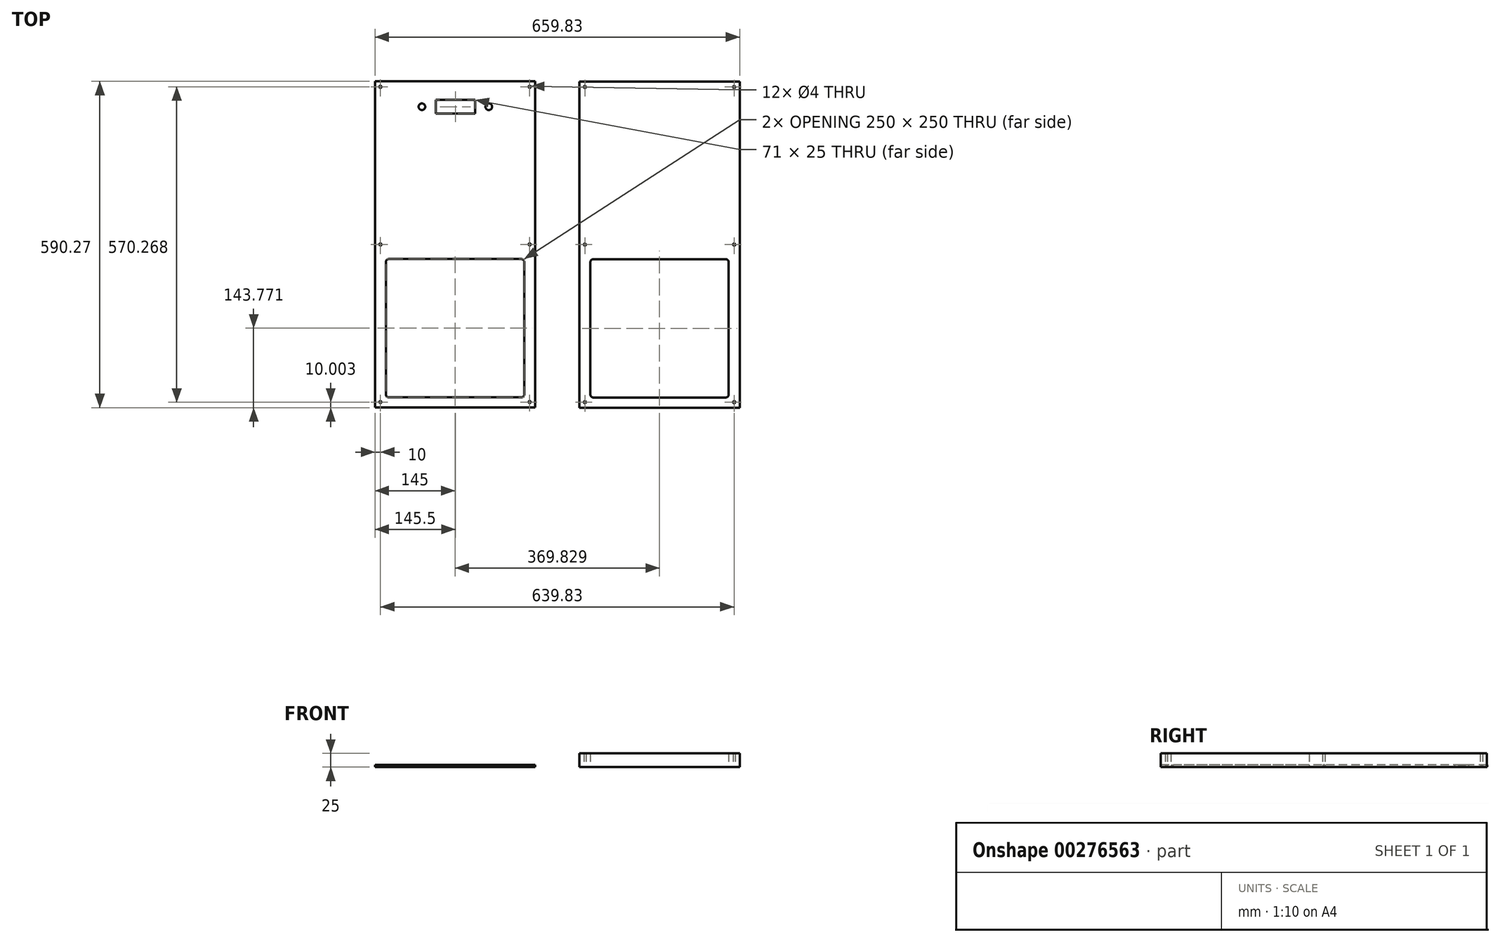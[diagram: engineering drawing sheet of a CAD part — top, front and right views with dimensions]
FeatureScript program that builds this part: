
annotation { "Feature Type Name" : "Feature", "Feature Type Description" : "" }
export const myFeature = defineFeature(function(context is Context, id is Id, definition is map)
    precondition{}
    {
        {
            var Q0;
            Q0=qCreatedBy(makeId("Top.planeOp"),FACE);
            var sketch = newSketch(context, id + "F0", { "sketchPlane" : qUnion([Q0])});
            skLineSegment(sketch, "E0.bottom", {"start": v(-206, 398.8) * mm, "end": v(84, 398.8) * mm});
            skLineSegment(sketch, "E0.top", {"start": v(-206, -191.2) * mm, "end": v(84, -191.2) * mm});
            skLineSegment(sketch, "E0.left", {"start": v(-206, 398.8) * mm, "end": v(-206, -191.2) * mm});
            skLineSegment(sketch, "E0.right", {"start": v(84, 398.8) * mm, "end": v(84, -191.2) * mm});
            skLineSegment(sketch, "E1.bottom", {"start": v(-186, 77.3) * mm, "end": v(64, 77.3) * mm});
            skLineSegment(sketch, "E1.top", {"start": v(-186, -172.7) * mm, "end": v(64, -172.7) * mm});
            skLineSegment(sketch, "E1.left", {"start": v(-186, 77.3) * mm, "end": v(-186, -172.7) * mm});
            skLineSegment(sketch, "E1.right", {"start": v(64, 77.3) * mm, "end": v(64, -172.7) * mm});
            skLineSegment(sketch, "E2.bottom", {"start": v(-96, 365.3) * mm, "end": v(-25, 365.3) * mm});
            skLineSegment(sketch, "E2.top", {"start": v(-96, 340.3) * mm, "end": v(-25, 340.3) * mm});
            skLineSegment(sketch, "E2.left", {"start": v(-96, 365.3) * mm, "end": v(-96, 340.3) * mm});
            skLineSegment(sketch, "E2.right", {"start": v(-25, 365.3) * mm, "end": v(-25, 340.3) * mm});
            skCircle(sketch, "E3", {"center": v(0, 352.8) * mm, "radius": 6 * mm});
            skCircle(sketch, "E4", {"center": v(-121, 352.8) * mm, "radius": 6 * mm});
            skSolve(sketch);
        }
        {
            var Q0;
            Q0 = qSketchRegion(id + "F0", true);
            extrude(context, id + "F1", {"entities" : qUnion([Q0]), "depth" : 4 * mm, "offsetDistance" : 25 * mm});
        }
        {
            var Q0;
            Q0=makeQuery(id+"F1.opExtrude","CAP_FACE",FACE,{"disambiguationData":[OSD([sQuery(id+"F0.wireOp",EDGE,"E0.bottom"),sQuery(id+"F0.wireOp",EDGE,"E0.top"),sQuery(id+"F0.wireOp",EDGE,"E0.left"),sQuery(id+"F0.wireOp",EDGE,"E0.right"),sQuery(id+"F0.wireOp",EDGE,"E1.bottom"),sQuery(id+"F0.wireOp",EDGE,"E1.top"),sQuery(id+"F0.wireOp",EDGE,"E1.left"),sQuery(id+"F0.wireOp",EDGE,"E1.right"),sQuery(id+"F0.wireOp",EDGE,"E2.bottom"),sQuery(id+"F0.wireOp",EDGE,"E2.top"),sQuery(id+"F0.wireOp",EDGE,"E2.left"),sQuery(id+"F0.wireOp",EDGE,"E2.right"),sQuery(id+"F0.wireOp",EDGE,"E3"),sQuery(id+"F0.wireOp",EDGE,"E4")])],"isStart":false});
            var sketch = newSketch(context, id + "F2", { "sketchPlane" : qUnion([Q0])});
            skPoint(sketch, "E5", {"position": v(-196, -181.2) * mm});
            skPoint(sketch, "E6", {"position": v(74, -181.2) * mm});
            skPoint(sketch, "E7", {"position": v(74, 103.8) * mm});
            skPoint(sketch, "E8", {"position": v(74, 388.8) * mm});
            skPoint(sketch, "E9", {"position": v(-196, 103.8) * mm});
            skPoint(sketch, "E10", {"position": v(-196, 388.8) * mm});
            skSolve(sketch);
        }
        {
            var Q0;
            Q0=sQuery(id+"F2.wireOp",VERTEX,"E10");
            var Q1;
            Q1=sQuery(id+"F2.wireOp",VERTEX,"E8");
            var Q2;
            Q2=sQuery(id+"F2.wireOp",VERTEX,"E7");
            var Q3;
            Q3=sQuery(id+"F2.wireOp",VERTEX,"E9");
            var Q4;
            Q4=sQuery(id+"F2.wireOp",VERTEX,"E5");
            var Q5;
            Q5=sQuery(id+"F2.wireOp",VERTEX,"E6");
            var Q6;
            Q6=makeQuery(id+"F1.opExtrude","SWEPT_BODY",BODY,{"disambiguationData":[OSD([sQuery(id+"F0.wireOp",EDGE,"E0.bottom"),sQuery(id+"F0.wireOp",EDGE,"E0.top"),sQuery(id+"F0.wireOp",EDGE,"E0.left"),sQuery(id+"F0.wireOp",EDGE,"E0.right"),sQuery(id+"F0.wireOp",EDGE,"E1.bottom"),sQuery(id+"F0.wireOp",EDGE,"E1.top"),sQuery(id+"F0.wireOp",EDGE,"E1.left"),sQuery(id+"F0.wireOp",EDGE,"E1.right"),sQuery(id+"F0.wireOp",EDGE,"E2.bottom"),sQuery(id+"F0.wireOp",EDGE,"E2.top"),sQuery(id+"F0.wireOp",EDGE,"E2.left"),sQuery(id+"F0.wireOp",EDGE,"E2.right"),sQuery(id+"F0.wireOp",EDGE,"E3"),sQuery(id+"F0.wireOp",EDGE,"E4")])]});
            hole(context, id + "F3", {"style" : HoleStyle.SIMPLE, "endStyle" : HoleEndStyle.THROUGH, "holeDiameter" : 4 * mm, "majorDiameter" : 5 * mm, "tappedDepth" : 12 * mm, "tapClearance" : 3, "locations" : qUnion([Q0, Q1, Q2, Q3, Q4, Q5]), "scope" : qUnion([Q6])});
        }
        {
            var Q0;
            Q0=qCreatedBy(makeId("Top.planeOp"),FACE);
            var sketch = newSketch(context, id + "F4", { "sketchPlane" : qUnion([Q0])});
            skLineSegment(sketch, "E11.bottom", {"start": v(163.83, 398.53) * mm, "end": v(453.83, 398.53) * mm});
            skLineSegment(sketch, "E11.top", {"start": v(163.83, -191.47) * mm, "end": v(453.83, -191.47) * mm});
            skLineSegment(sketch, "E11.left", {"start": v(163.83, 398.53) * mm, "end": v(163.83, -191.47) * mm});
            skLineSegment(sketch, "E11.right", {"start": v(453.83, 398.53) * mm, "end": v(453.83, -191.47) * mm});
            skLineSegment(sketch, "E12.bottom", {"start": v(183.83, 77.03) * mm, "end": v(433.83, 77.03) * mm});
            skLineSegment(sketch, "E12.top", {"start": v(183.83, -172.97) * mm, "end": v(433.83, -172.97) * mm});
            skLineSegment(sketch, "E12.left", {"start": v(183.83, 77.03) * mm, "end": v(183.83, -172.97) * mm});
            skLineSegment(sketch, "E12.right", {"start": v(433.83, 77.03) * mm, "end": v(433.83, -172.97) * mm});
            skPoint(sketch, "E13", {"position": v(173.83, 103.53) * mm});
            skSolve(sketch);
        }
        {
            var Q0;
            Q0 = qSketchRegion(id + "F4", true);
            extrude(context, id + "F5", {"entities" : qUnion([Q0]), "depth" : 25 * mm, "offsetDistance" : 25 * mm});
        }
        {
            var Q0;
            Q0=makeQuery(id+"F5.opExtrude","CAP_FACE",FACE,{"disambiguationData":[OSD([sQuery(id+"F4.wireOp",EDGE,"E11.bottom"),sQuery(id+"F4.wireOp",EDGE,"E11.top"),sQuery(id+"F4.wireOp",EDGE,"E11.left"),sQuery(id+"F4.wireOp",EDGE,"E11.right"),sQuery(id+"F4.wireOp",EDGE,"E12.bottom"),sQuery(id+"F4.wireOp",EDGE,"E12.top"),sQuery(id+"F4.wireOp",EDGE,"E12.left"),sQuery(id+"F4.wireOp",EDGE,"E12.right")])],"isStart":false});
            var sketch = newSketch(context, id + "F6", { "sketchPlane" : qUnion([Q0])});
            skPoint(sketch, "E14", {"position": v(173.83, 388.53) * mm});
            skPoint(sketch, "E15", {"position": v(443.83, 388.53) * mm});
            skPoint(sketch, "E16", {"position": v(443.83, 103.53) * mm});
            skPoint(sketch, "E17", {"position": v(443.83, -181.47) * mm});
            skPoint(sketch, "E18", {"position": v(173.83, -181.47) * mm});
            skPoint(sketch, "E19", {"position": v(173.83, 103.53) * mm});
            skSolve(sketch);
        }
        {
            var Q0;
            Q0=sQuery(id+"F6.wireOp",VERTEX,"E14");
            var Q1;
            Q1=sQuery(id+"F6.wireOp",VERTEX,"E15");
            var Q2;
            Q2=sQuery(id+"F6.wireOp",VERTEX,"E16");
            var Q3;
            Q3=sQuery(id+"F6.wireOp",VERTEX,"E19");
            var Q4;
            Q4=sQuery(id+"F6.wireOp",VERTEX,"E18");
            var Q5;
            Q5=sQuery(id+"F6.wireOp",VERTEX,"E17");
            var Q6;
            Q6=makeQuery(id+"F5.opExtrude","SWEPT_BODY",BODY,{"disambiguationData":[OSD([sQuery(id+"F4.wireOp",EDGE,"E11.bottom"),sQuery(id+"F4.wireOp",EDGE,"E11.top"),sQuery(id+"F4.wireOp",EDGE,"E11.left"),sQuery(id+"F4.wireOp",EDGE,"E11.right"),sQuery(id+"F4.wireOp",EDGE,"E12.bottom"),sQuery(id+"F4.wireOp",EDGE,"E12.top"),sQuery(id+"F4.wireOp",EDGE,"E12.left"),sQuery(id+"F4.wireOp",EDGE,"E12.right")])]});
            hole(context, id + "F7", {"style" : HoleStyle.SIMPLE, "endStyle" : HoleEndStyle.THROUGH, "holeDiameter" : 4 * mm, "majorDiameter" : 5 * mm, "tappedDepth" : 12 * mm, "tapClearance" : 3, "locations" : qUnion([Q0, Q1, Q2, Q3, Q4, Q5]), "scope" : qUnion([Q6])});
        }
        {
            var Q0;
            Q0=makeQuery(id+"F5.opExtrude","SWEPT_EDGE",EDGE,{"disambiguationData":[OSD([sQuery(id+"F4.wireOp",EDGE,"E12.bottom"),sQuery(id+"F4.wireOp",EDGE,"E12.right")])]});
            var Q1;
            Q1=makeQuery(id+"F5.opExtrude","SWEPT_EDGE",EDGE,{"disambiguationData":[OSD([sQuery(id+"F4.wireOp",EDGE,"E12.bottom"),sQuery(id+"F4.wireOp",EDGE,"E12.left")])]});
            var Q2;
            Q2=makeQuery(id+"F5.opExtrude","SWEPT_EDGE",EDGE,{"disambiguationData":[OSD([sQuery(id+"F4.wireOp",EDGE,"E12.top"),sQuery(id+"F4.wireOp",EDGE,"E12.right")])]});
            var Q3;
            Q3=makeQuery(id+"F5.opExtrude","SWEPT_EDGE",EDGE,{"disambiguationData":[OSD([sQuery(id+"F4.wireOp",EDGE,"E12.top"),sQuery(id+"F4.wireOp",EDGE,"E12.left")])]});
            fillet(context, id + "F8", {"entities" : qUnion([Q0, Q1, Q2, Q3]), "radius" : 5 * mm, "tangentPropagation" : true, "allowEdgeOverflow" : false});
        }
        {
            var Q0;
            Q0=makeQuery(id+"F1.opExtrude","SWEPT_EDGE",EDGE,{"disambiguationData":[OSD([sQuery(id+"F0.wireOp",EDGE,"E1.bottom"),sQuery(id+"F0.wireOp",EDGE,"E1.right")])]});
            var Q1;
            Q1=makeQuery(id+"F1.opExtrude","SWEPT_EDGE",EDGE,{"disambiguationData":[OSD([sQuery(id+"F0.wireOp",EDGE,"E1.bottom"),sQuery(id+"F0.wireOp",EDGE,"E1.left")])]});
            var Q2;
            Q2=makeQuery(id+"F1.opExtrude","SWEPT_EDGE",EDGE,{"disambiguationData":[OSD([sQuery(id+"F0.wireOp",EDGE,"E1.top"),sQuery(id+"F0.wireOp",EDGE,"E1.right")])]});
            var Q3;
            Q3=makeQuery(id+"F1.opExtrude","SWEPT_EDGE",EDGE,{"disambiguationData":[OSD([sQuery(id+"F0.wireOp",EDGE,"E1.top"),sQuery(id+"F0.wireOp",EDGE,"E1.left")])]});
            fillet(context, id + "F9", {"entities" : qUnion([Q0, Q1, Q2, Q3]), "radius" : 5 * mm, "tangentPropagation" : true, "allowEdgeOverflow" : false});
        }
    });
